# Revit family: Elan_Bing_Round_CoffeeTable
name_source: partatom
category: Furniture
revit_build: Autodesk Revit Architecture 2015 (Build: 20141119_0715(x64)
units: mm (PartAtom-declared; Revit-internal decimal feet)

## types (6) — shared parameters
Assembly Code = E2020200
Assembly Description = Furniture & Accessories
Description = Bing Coffee Table
Height = 1' - 3"
Manufacturer = Decca Elan
Product URL = http://elanbydecca.com
URL = http://elanbydecca.com

## per-type parameters (varying)
| type | Depth | L30 | L36 | L42 | Model | Width |
| 36" | 3' - 0" | No | No | No | FT CT115 | 3' - 0" |
| 36" (Layup) | 3' - 0" | No | Yes | No | FT CT115B | 3' - 0" |
| 30" (Layup) | 2' - 6" | Yes | No | No | FT CT135B | 2' - 6" |
| 30" | 2' - 6" | No | No | No | FT CT135 | 2' - 6" |
| 42" | 3' - 6" | No | No | No | FT CT120 | 3' - 6" |
| 42" (Layup) | 3' - 6" | No | No | Yes | FT CT120B | 3' - 6" |

## geometry (parser evidence)
native form markers: Sweep x3
no freeform markers — native parametric forms only
